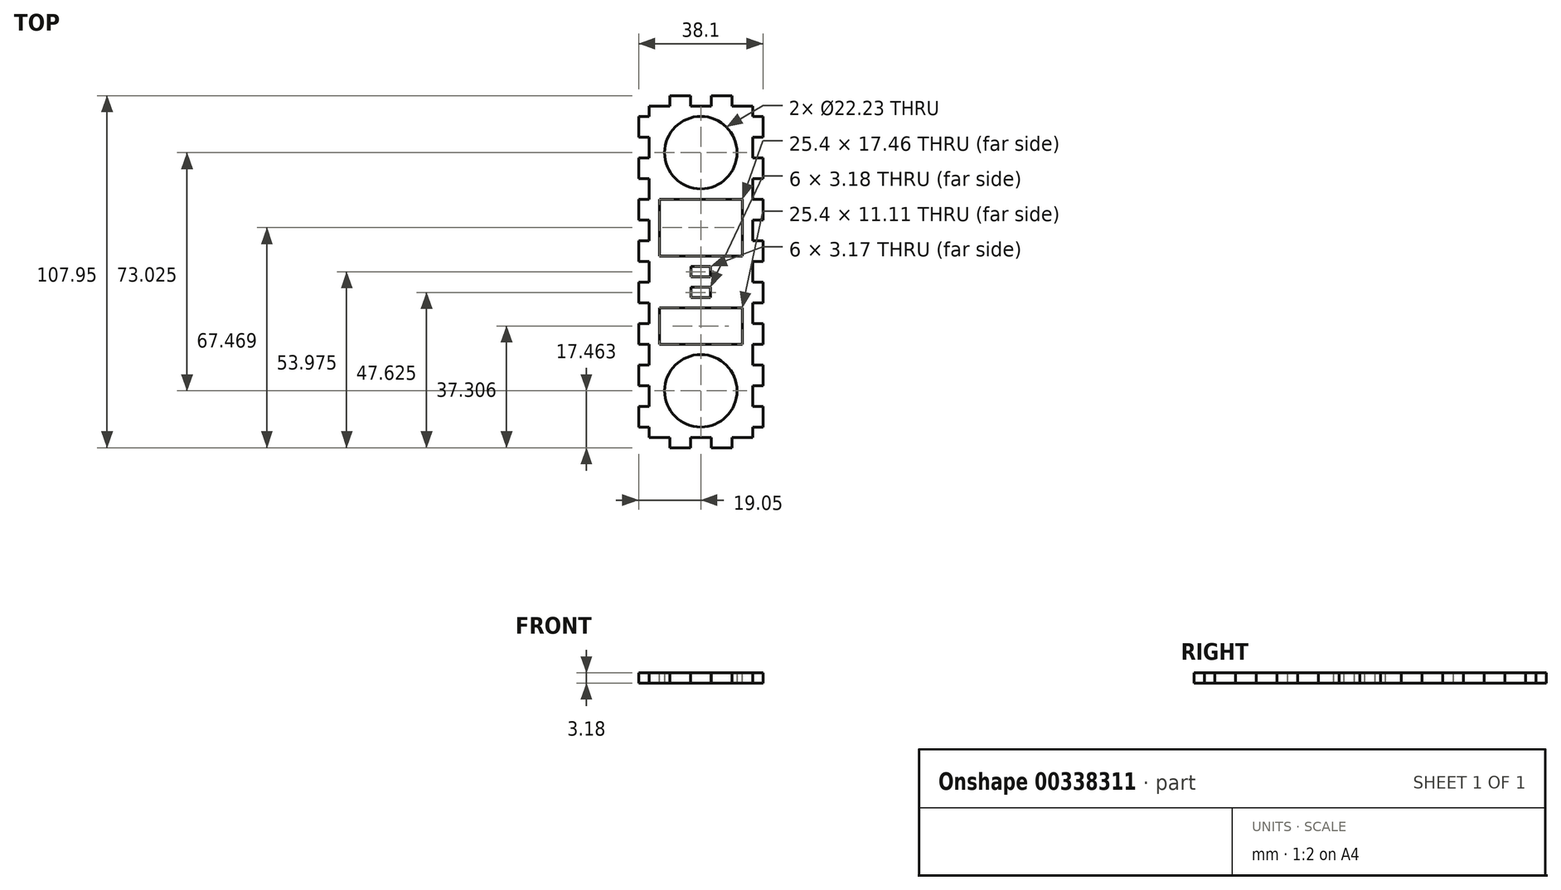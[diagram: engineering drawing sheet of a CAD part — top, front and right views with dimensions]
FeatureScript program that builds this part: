
annotation { "Feature Type Name" : "Feature", "Feature Type Description" : "" }
export const myFeature = defineFeature(function(context is Context, id is Id, definition is map)
    precondition{}
    {
        {
            var Q0;
            Q0=qCreatedBy(makeId("Top.planeOp"),FACE);
            var sketch = newSketch(context, id + "F0", { "sketchPlane" : qUnion([Q0])});
            skLineSegment(sketch, "E0.bottom", {"start": v(0, 0) * mm, "end": v(38.1, 0) * mm});
            skLineSegment(sketch, "E0.top", {"start": v(0, -107.95) * mm, "end": v(38.1, -107.95) * mm});
            skLineSegment(sketch, "E0.left", {"start": v(0, 0) * mm, "end": v(0, -107.95) * mm});
            skLineSegment(sketch, "E0.right", {"start": v(38.1, 0) * mm, "end": v(38.1, -107.95) * mm});
            skLineSegment(sketch, "E1", {"start": v(19.05, 0) * mm, "end": v(19.05, -17.46) * mm, "construction": true});
            skCircle(sketch, "E2", {"center": v(19.05, -17.46) * mm, "radius": 11.11 * mm});
            skLineSegment(sketch, "E3", {"start": v(19.05, -17.46) * mm, "end": v(19.05, -90.49) * mm, "construction": true});
            skLineSegment(sketch, "E4", {"start": v(19.05, -90.49) * mm, "end": v(19.05, -107.95) * mm, "construction": true});
            skCircle(sketch, "E5", {"center": v(19.05, -90.49) * mm, "radius": 11.11 * mm});
            skSolve(sketch);
        }
        {
            var Q0;
            Q0=qSketchRegion(id+"F0",true);
            extrude(context, id + "F1", {"entities" : qUnion([Q0]), "depth" : 3.17 * mm});
        }
        {
            var Q0;
            Q0=makeQuery(id+"F1.opExtrude","CAP_FACE",FACE,{"disambiguationData":[OSD([sQuery(id+"F0.wireOp",EDGE,"E0.bottom"),sQuery(id+"F0.wireOp",EDGE,"E0.top"),sQuery(id+"F0.wireOp",EDGE,"E0.left"),sQuery(id+"F0.wireOp",EDGE,"E0.right"),sQuery(id+"F0.wireOp",EDGE,"E2"),sQuery(id+"F0.wireOp",EDGE,"E5")])],"isStart":false});
            var sketch = newSketch(context, id + "F2", { "sketchPlane" : qUnion([Q0])});
            skLineSegment(sketch, "E6.bottom", {"start": v(38.1, 0) * mm, "end": v(34.93, 0) * mm});
            skLineSegment(sketch, "E6.top", {"start": v(38.1, -6.35) * mm, "end": v(34.93, -6.35) * mm});
            skLineSegment(sketch, "E6.left", {"start": v(38.1, 0) * mm, "end": v(38.1, -6.35) * mm});
            skLineSegment(sketch, "E6.right", {"start": v(34.93, 0) * mm, "end": v(34.93, -6.35) * mm});
            skLineSegment(sketch, "E7.bottom", {"start": v(0, 0) * mm, "end": v(3.17, 0) * mm});
            skLineSegment(sketch, "E7.top", {"start": v(0, -6.35) * mm, "end": v(3.17, -6.35) * mm});
            skLineSegment(sketch, "E7.left", {"start": v(0, 0) * mm, "end": v(0, -6.35) * mm});
            skLineSegment(sketch, "E7.right", {"start": v(3.17, 0) * mm, "end": v(3.17, -6.35) * mm});
            skLineSegment(sketch, "E8", {"start": v(3.17, -6.35) * mm, "end": v(3.17, -12.7) * mm, "construction": true});
            skLineSegment(sketch, "E9.bottom", {"start": v(3.17, -12.7) * mm, "end": v(0, -12.7) * mm});
            skLineSegment(sketch, "E9.top", {"start": v(3.17, -19.05) * mm, "end": v(0, -19.05) * mm});
            skLineSegment(sketch, "E9.left", {"start": v(3.17, -12.7) * mm, "end": v(3.17, -19.05) * mm});
            skLineSegment(sketch, "E9.right", {"start": v(0, -12.7) * mm, "end": v(0, -19.05) * mm});
            skLineSegment(sketch, "E10", {"start": v(34.93, -6.35) * mm, "end": v(34.93, -12.7) * mm, "construction": true});
            skLineSegment(sketch, "E11.bottom", {"start": v(34.93, -12.7) * mm, "end": v(38.1, -12.7) * mm});
            skLineSegment(sketch, "E11.top", {"start": v(34.93, -19.05) * mm, "end": v(38.1, -19.05) * mm});
            skLineSegment(sketch, "E11.left", {"start": v(34.93, -12.7) * mm, "end": v(34.93, -19.05) * mm});
            skLineSegment(sketch, "E11.right", {"start": v(38.1, -12.7) * mm, "end": v(38.1, -19.05) * mm});
            skLineSegment(sketch, "E12.0.1.0", {"start": v(34.93, -25.4) * mm, "end": v(38.1, -25.4) * mm});
            skLineSegment(sketch, "E12.0.1.1", {"start": v(34.93, -31.75) * mm, "end": v(38.1, -31.75) * mm});
            skLineSegment(sketch, "E12.0.1.2", {"start": v(34.93, -19.05) * mm, "end": v(34.93, -25.4) * mm, "construction": true});
            skLineSegment(sketch, "E12.0.1.3", {"start": v(38.1, -25.4) * mm, "end": v(38.1, -31.75) * mm});
            skLineSegment(sketch, "E12.0.1.4", {"start": v(34.93, -25.4) * mm, "end": v(34.93, -31.75) * mm});
            skLineSegment(sketch, "E12.0.2.0", {"start": v(34.93, -38.1) * mm, "end": v(38.1, -38.1) * mm});
            skLineSegment(sketch, "E12.0.2.1", {"start": v(34.93, -44.45) * mm, "end": v(38.1, -44.45) * mm});
            skLineSegment(sketch, "E12.0.2.2", {"start": v(34.93, -31.75) * mm, "end": v(34.93, -38.1) * mm, "construction": true});
            skLineSegment(sketch, "E12.0.2.3", {"start": v(38.1, -38.1) * mm, "end": v(38.1, -44.45) * mm});
            skLineSegment(sketch, "E12.0.2.4", {"start": v(34.93, -38.1) * mm, "end": v(34.93, -44.45) * mm});
            skLineSegment(sketch, "E12.0.3.0", {"start": v(34.93, -50.8) * mm, "end": v(38.1, -50.8) * mm});
            skLineSegment(sketch, "E12.0.3.1", {"start": v(34.93, -57.15) * mm, "end": v(38.1, -57.15) * mm});
            skLineSegment(sketch, "E12.0.3.2", {"start": v(34.93, -44.45) * mm, "end": v(34.93, -50.8) * mm, "construction": true});
            skLineSegment(sketch, "E12.0.3.3", {"start": v(38.1, -50.8) * mm, "end": v(38.1, -57.15) * mm});
            skLineSegment(sketch, "E12.0.3.4", {"start": v(34.93, -50.8) * mm, "end": v(34.93, -57.15) * mm});
            skLineSegment(sketch, "E12.0.4.0", {"start": v(34.93, -63.5) * mm, "end": v(38.1, -63.5) * mm});
            skLineSegment(sketch, "E12.0.4.1", {"start": v(34.93, -69.85) * mm, "end": v(38.1, -69.85) * mm});
            skLineSegment(sketch, "E12.0.4.2", {"start": v(34.93, -57.15) * mm, "end": v(34.93, -63.5) * mm, "construction": true});
            skLineSegment(sketch, "E12.0.4.3", {"start": v(38.1, -63.5) * mm, "end": v(38.1, -69.85) * mm});
            skLineSegment(sketch, "E12.0.4.4", {"start": v(34.93, -63.5) * mm, "end": v(34.93, -69.85) * mm});
            skLineSegment(sketch, "E12.0.5.0", {"start": v(34.93, -76.2) * mm, "end": v(38.1, -76.2) * mm});
            skLineSegment(sketch, "E12.0.5.1", {"start": v(34.93, -82.55) * mm, "end": v(38.1, -82.55) * mm});
            skLineSegment(sketch, "E12.0.5.2", {"start": v(34.93, -69.85) * mm, "end": v(34.93, -76.2) * mm, "construction": true});
            skLineSegment(sketch, "E12.0.5.3", {"start": v(38.1, -76.2) * mm, "end": v(38.1, -82.55) * mm});
            skLineSegment(sketch, "E12.0.5.4", {"start": v(34.93, -76.2) * mm, "end": v(34.93, -82.55) * mm});
            skLineSegment(sketch, "E12.0.6.0", {"start": v(34.93, -88.9) * mm, "end": v(38.1, -88.9) * mm});
            skLineSegment(sketch, "E12.0.6.1", {"start": v(34.93, -95.25) * mm, "end": v(38.1, -95.25) * mm});
            skLineSegment(sketch, "E12.0.6.2", {"start": v(34.93, -82.55) * mm, "end": v(34.93, -88.9) * mm, "construction": true});
            skLineSegment(sketch, "E12.0.6.3", {"start": v(38.1, -88.9) * mm, "end": v(38.1, -95.25) * mm});
            skLineSegment(sketch, "E12.0.6.4", {"start": v(34.93, -88.9) * mm, "end": v(34.93, -95.25) * mm});
            skLineSegment(sketch, "E12.0.7.0", {"start": v(34.93, -101.6) * mm, "end": v(38.1, -101.6) * mm});
            skLineSegment(sketch, "E12.0.7.1", {"start": v(34.93, -107.95) * mm, "end": v(38.1, -107.95) * mm});
            skLineSegment(sketch, "E12.0.7.2", {"start": v(34.93, -95.25) * mm, "end": v(34.93, -101.6) * mm, "construction": true});
            skLineSegment(sketch, "E12.0.7.3", {"start": v(38.1, -101.6) * mm, "end": v(38.1, -107.95) * mm});
            skLineSegment(sketch, "E12.0.7.4", {"start": v(34.93, -101.6) * mm, "end": v(34.93, -107.95) * mm});
            skLineSegment(sketch, "E12.0.8.0", {"start": v(34.93, -114.3) * mm, "end": v(38.1, -114.3) * mm});
            skLineSegment(sketch, "E12.0.8.1", {"start": v(34.93, -120.65) * mm, "end": v(38.1, -120.65) * mm});
            skLineSegment(sketch, "E12.0.8.2", {"start": v(34.93, -107.95) * mm, "end": v(34.93, -114.3) * mm, "construction": true});
            skLineSegment(sketch, "E12.0.8.3", {"start": v(38.1, -114.3) * mm, "end": v(38.1, -120.65) * mm});
            skLineSegment(sketch, "E12.0.8.4", {"start": v(34.93, -114.3) * mm, "end": v(34.93, -120.65) * mm});
            skLineSegment(sketch, "E12.0.9.0", {"start": v(34.93, -127) * mm, "end": v(38.1, -127) * mm});
            skLineSegment(sketch, "E12.0.9.1", {"start": v(34.93, -133.35) * mm, "end": v(38.1, -133.35) * mm});
            skLineSegment(sketch, "E12.0.9.2", {"start": v(34.93, -120.65) * mm, "end": v(34.93, -127) * mm, "construction": true});
            skLineSegment(sketch, "E12.0.9.3", {"start": v(38.1, -127) * mm, "end": v(38.1, -133.35) * mm});
            skLineSegment(sketch, "E12.0.9.4", {"start": v(34.93, -127) * mm, "end": v(34.93, -133.35) * mm});
            skLineSegment(sketch, "E12.direction1", {"start": v(17.46, -19.05) * mm, "end": v(34.93, -19.05) * mm, "construction": true});
            skLineSegment(sketch, "E12.direction2", {"start": v(34.93, -19.05) * mm, "end": v(34.93, -31.75) * mm, "construction": true});
            skLineSegment(sketch, "E13.0.1.0", {"start": v(3.17, -19.05) * mm, "end": v(3.17, -25.4) * mm, "construction": true});
            skLineSegment(sketch, "E13.0.1.1", {"start": v(3.17, -25.4) * mm, "end": v(0, -25.4) * mm});
            skLineSegment(sketch, "E13.0.1.2", {"start": v(3.17, -31.75) * mm, "end": v(0, -31.75) * mm});
            skLineSegment(sketch, "E13.0.1.3", {"start": v(3.17, -25.4) * mm, "end": v(3.17, -31.75) * mm});
            skLineSegment(sketch, "E13.0.1.4", {"start": v(0, -25.4) * mm, "end": v(0, -31.75) * mm});
            skLineSegment(sketch, "E13.0.2.0", {"start": v(3.17, -31.75) * mm, "end": v(3.17, -38.1) * mm, "construction": true});
            skLineSegment(sketch, "E13.0.2.1", {"start": v(3.17, -38.1) * mm, "end": v(0, -38.1) * mm});
            skLineSegment(sketch, "E13.0.2.2", {"start": v(3.17, -44.45) * mm, "end": v(0, -44.45) * mm});
            skLineSegment(sketch, "E13.0.2.3", {"start": v(3.17, -38.1) * mm, "end": v(3.17, -44.45) * mm});
            skLineSegment(sketch, "E13.0.2.4", {"start": v(0, -38.1) * mm, "end": v(0, -44.45) * mm});
            skLineSegment(sketch, "E13.0.3.0", {"start": v(3.17, -44.45) * mm, "end": v(3.17, -50.8) * mm, "construction": true});
            skLineSegment(sketch, "E13.0.3.1", {"start": v(3.17, -50.8) * mm, "end": v(0, -50.8) * mm});
            skLineSegment(sketch, "E13.0.3.2", {"start": v(3.17, -57.15) * mm, "end": v(0, -57.15) * mm});
            skLineSegment(sketch, "E13.0.3.3", {"start": v(3.17, -50.8) * mm, "end": v(3.17, -57.15) * mm});
            skLineSegment(sketch, "E13.0.3.4", {"start": v(0, -50.8) * mm, "end": v(0, -57.15) * mm});
            skLineSegment(sketch, "E13.0.4.0", {"start": v(3.17, -57.15) * mm, "end": v(3.17, -63.5) * mm, "construction": true});
            skLineSegment(sketch, "E13.0.4.1", {"start": v(3.17, -63.5) * mm, "end": v(0, -63.5) * mm});
            skLineSegment(sketch, "E13.0.4.2", {"start": v(3.17, -69.85) * mm, "end": v(0, -69.85) * mm});
            skLineSegment(sketch, "E13.0.4.3", {"start": v(3.17, -63.5) * mm, "end": v(3.17, -69.85) * mm});
            skLineSegment(sketch, "E13.0.4.4", {"start": v(0, -63.5) * mm, "end": v(0, -69.85) * mm});
            skLineSegment(sketch, "E13.0.5.0", {"start": v(3.17, -69.85) * mm, "end": v(3.17, -76.2) * mm, "construction": true});
            skLineSegment(sketch, "E13.0.5.1", {"start": v(3.17, -76.2) * mm, "end": v(0, -76.2) * mm});
            skLineSegment(sketch, "E13.0.5.2", {"start": v(3.17, -82.55) * mm, "end": v(0, -82.55) * mm});
            skLineSegment(sketch, "E13.0.5.3", {"start": v(3.17, -76.2) * mm, "end": v(3.17, -82.55) * mm});
            skLineSegment(sketch, "E13.0.5.4", {"start": v(0, -76.2) * mm, "end": v(0, -82.55) * mm});
            skLineSegment(sketch, "E13.0.6.0", {"start": v(3.17, -82.55) * mm, "end": v(3.17, -88.9) * mm, "construction": true});
            skLineSegment(sketch, "E13.0.6.1", {"start": v(3.17, -88.9) * mm, "end": v(0, -88.9) * mm});
            skLineSegment(sketch, "E13.0.6.2", {"start": v(3.17, -95.25) * mm, "end": v(0, -95.25) * mm});
            skLineSegment(sketch, "E13.0.6.3", {"start": v(3.17, -88.9) * mm, "end": v(3.17, -95.25) * mm});
            skLineSegment(sketch, "E13.0.6.4", {"start": v(0, -88.9) * mm, "end": v(0, -95.25) * mm});
            skLineSegment(sketch, "E13.0.7.0", {"start": v(3.17, -95.25) * mm, "end": v(3.17, -101.6) * mm, "construction": true});
            skLineSegment(sketch, "E13.0.7.1", {"start": v(3.17, -101.6) * mm, "end": v(0, -101.6) * mm});
            skLineSegment(sketch, "E13.0.7.2", {"start": v(3.17, -107.95) * mm, "end": v(0, -107.95) * mm});
            skLineSegment(sketch, "E13.0.7.3", {"start": v(3.17, -101.6) * mm, "end": v(3.17, -107.95) * mm});
            skLineSegment(sketch, "E13.0.7.4", {"start": v(0, -101.6) * mm, "end": v(0, -107.95) * mm});
            skLineSegment(sketch, "E13.0.8.0", {"start": v(3.17, -107.95) * mm, "end": v(3.17, -114.3) * mm, "construction": true});
            skLineSegment(sketch, "E13.0.8.1", {"start": v(3.17, -114.3) * mm, "end": v(0, -114.3) * mm});
            skLineSegment(sketch, "E13.0.8.2", {"start": v(3.17, -120.65) * mm, "end": v(0, -120.65) * mm});
            skLineSegment(sketch, "E13.0.8.3", {"start": v(3.17, -114.3) * mm, "end": v(3.17, -120.65) * mm});
            skLineSegment(sketch, "E13.0.8.4", {"start": v(0, -114.3) * mm, "end": v(0, -120.65) * mm});
            skLineSegment(sketch, "E13.0.9.0", {"start": v(3.17, -120.65) * mm, "end": v(3.17, -127) * mm, "construction": true});
            skLineSegment(sketch, "E13.0.9.1", {"start": v(3.17, -127) * mm, "end": v(0, -127) * mm});
            skLineSegment(sketch, "E13.0.9.2", {"start": v(3.17, -133.35) * mm, "end": v(0, -133.35) * mm});
            skLineSegment(sketch, "E13.0.9.3", {"start": v(3.17, -127) * mm, "end": v(3.17, -133.35) * mm});
            skLineSegment(sketch, "E13.0.9.4", {"start": v(0, -127) * mm, "end": v(0, -133.35) * mm});
            skLineSegment(sketch, "E13.direction1", {"start": v(0, -19.05) * mm, "end": v(17.46, -19.05) * mm, "construction": true});
            skLineSegment(sketch, "E13.direction2", {"start": v(0, -19.05) * mm, "end": v(0, -31.75) * mm, "construction": true});
            skLineSegment(sketch, "E14", {"start": v(19.05, 0) * mm, "end": v(19.05, -17.46) * mm, "construction": true});
            skLineSegment(sketch, "E15", {"start": v(19.05, -17.46) * mm, "end": v(19.05, -31.75) * mm, "construction": true});
            skLineSegment(sketch, "E16.bottom", {"start": v(6.35, -31.75) * mm, "end": v(31.75, -31.75) * mm});
            skLineSegment(sketch, "E16.left", {"start": v(6.35, -31.75) * mm, "end": v(6.35, -49.21) * mm});
            skLineSegment(sketch, "E16.right", {"start": v(31.75, -31.75) * mm, "end": v(31.75, -49.21) * mm});
            skLineSegment(sketch, "E17", {"start": v(31.75, -40.48) * mm, "end": v(34.93, -40.48) * mm, "construction": true});
            skLineSegment(sketch, "E18", {"start": v(19.05, -76.2) * mm, "end": v(19.05, -90.49) * mm, "construction": true});
            skLineSegment(sketch, "E19", {"start": v(19.05, -90.49) * mm, "end": v(19.05, -107.95) * mm, "construction": true});
            skLineSegment(sketch, "E20", {"start": v(6.35, -49.21) * mm, "end": v(31.75, -49.21) * mm});
            skLineSegment(sketch, "E21.bottom", {"start": v(16.05, -52.39) * mm, "end": v(22.05, -52.39) * mm});
            skLineSegment(sketch, "E21.top", {"start": v(16.05, -55.56) * mm, "end": v(22.05, -55.56) * mm});
            skLineSegment(sketch, "E21.left", {"start": v(16.05, -52.39) * mm, "end": v(16.05, -55.56) * mm});
            skLineSegment(sketch, "E21.right", {"start": v(22.05, -52.39) * mm, "end": v(22.05, -55.56) * mm});
            skLineSegment(sketch, "E22", {"start": v(19.05, -52.39) * mm, "end": v(19.05, -49.21) * mm, "construction": true});
            skLineSegment(sketch, "E23", {"start": v(19.05, -55.56) * mm, "end": v(19.05, -58.74) * mm, "construction": true});
            skLineSegment(sketch, "E24.bottom", {"start": v(16.05, -58.74) * mm, "end": v(22.05, -58.74) * mm});
            skLineSegment(sketch, "E24.top", {"start": v(16.05, -61.91) * mm, "end": v(22.05, -61.91) * mm});
            skLineSegment(sketch, "E24.left", {"start": v(16.05, -58.74) * mm, "end": v(16.05, -61.91) * mm});
            skLineSegment(sketch, "E24.right", {"start": v(22.05, -58.74) * mm, "end": v(22.05, -61.91) * mm});
            skLineSegment(sketch, "E25", {"start": v(22.05, -53.97) * mm, "end": v(92.08, -53.97) * mm});
            skLineSegment(sketch, "E26", {"start": v(19.05, -61.91) * mm, "end": v(19.05, -65.09) * mm, "construction": true});
            skLineSegment(sketch, "E27", {"start": v(19.05, -17.46) * mm, "end": v(92.08, -17.46) * mm, "construction": true});
            skLineSegment(sketch, "E28", {"start": v(92.08, -17.46) * mm, "end": v(92.08, -90.49) * mm, "construction": true});
            skLineSegment(sketch, "E29", {"start": v(92.08, -90.49) * mm, "end": v(19.05, -90.49) * mm, "construction": true});
            skLineSegment(sketch, "E30.bottom", {"start": v(6.35, -65.09) * mm, "end": v(31.75, -65.09) * mm});
            skLineSegment(sketch, "E30.top", {"start": v(6.35, -76.2) * mm, "end": v(31.75, -76.2) * mm});
            skLineSegment(sketch, "E30.left", {"start": v(6.35, -65.09) * mm, "end": v(6.35, -76.2) * mm});
            skLineSegment(sketch, "E30.right", {"start": v(31.75, -65.09) * mm, "end": v(31.75, -76.2) * mm});
            skSolve(sketch);
        }
        {
            var Q0;
            Q0=qSketchRegion(id+"F2",true);
            var Q1;
            Q1=makeQuery(id+"F1.opExtrude","CAP_FACE",FACE,{"disambiguationData":[OSD([sQuery(id+"F0.wireOp",EDGE,"E0.bottom"),sQuery(id+"F0.wireOp",EDGE,"E0.top"),sQuery(id+"F0.wireOp",EDGE,"E0.left"),sQuery(id+"F0.wireOp",EDGE,"E0.right"),sQuery(id+"F0.wireOp",EDGE,"E2"),sQuery(id+"F0.wireOp",EDGE,"E5")])],"isStart":true});
            extrude(context, id + "F3", {"entities" : qUnion([Q0]), "operationType" : NewBodyOperationType.REMOVE, "endBound" : BoundingType.UP_TO_SURFACE, "oppositeDirection" : true, "endBoundEntityFace" : qUnion([Q1]), "depth" : 25.4 * mm});
        }
        {
            var Q0;
            Q0=makeQuery(id+"F1.opExtrude","CAP_FACE",FACE,{"disambiguationData":[OSD([sQuery(id+"F0.wireOp",EDGE,"E0.bottom"),sQuery(id+"F0.wireOp",EDGE,"E0.top"),sQuery(id+"F0.wireOp",EDGE,"E0.left"),sQuery(id+"F0.wireOp",EDGE,"E0.right"),sQuery(id+"F0.wireOp",EDGE,"E2"),sQuery(id+"F0.wireOp",EDGE,"E5")])],"isStart":false});
            var sketch = newSketch(context, id + "F4", { "sketchPlane" : qUnion([Q0])});
            skLineSegment(sketch, "E31.bottom", {"start": v(15.88, 0) * mm, "end": v(22.23, 0) * mm});
            skLineSegment(sketch, "E31.top", {"start": v(15.88, -3.18) * mm, "end": v(22.23, -3.18) * mm});
            skLineSegment(sketch, "E31.left", {"start": v(15.88, 0) * mm, "end": v(15.88, -3.18) * mm});
            skLineSegment(sketch, "E31.right", {"start": v(22.23, 0) * mm, "end": v(22.23, -3.18) * mm});
            skLineSegment(sketch, "E32.bottom", {"start": v(28.58, 0) * mm, "end": v(34.93, 0) * mm});
            skLineSegment(sketch, "E32.top", {"start": v(28.58, -3.18) * mm, "end": v(34.93, -3.18) * mm});
            skLineSegment(sketch, "E32.left", {"start": v(28.58, 0) * mm, "end": v(28.58, -3.18) * mm});
            skLineSegment(sketch, "E32.right", {"start": v(34.93, 0) * mm, "end": v(34.93, -3.18) * mm});
            skLineSegment(sketch, "E33", {"start": v(15.88, -3.18) * mm, "end": v(9.53, -3.18) * mm, "construction": true});
            skLineSegment(sketch, "E34", {"start": v(28.58, -3.18) * mm, "end": v(22.23, -3.18) * mm, "construction": true});
            skLineSegment(sketch, "E35.bottom", {"start": v(9.53, -3.18) * mm, "end": v(3.17, -3.18) * mm});
            skLineSegment(sketch, "E35.top", {"start": v(9.53, 0) * mm, "end": v(3.17, 0) * mm});
            skLineSegment(sketch, "E35.left", {"start": v(9.53, -3.18) * mm, "end": v(9.53, 0) * mm});
            skLineSegment(sketch, "E35.right", {"start": v(3.17, -3.18) * mm, "end": v(3.17, 0) * mm});
            skLineSegment(sketch, "E36.bottom", {"start": v(34.93, -107.95) * mm, "end": v(28.58, -107.95) * mm});
            skLineSegment(sketch, "E36.top", {"start": v(34.93, -104.78) * mm, "end": v(28.58, -104.78) * mm});
            skLineSegment(sketch, "E36.left", {"start": v(34.93, -107.95) * mm, "end": v(34.93, -104.78) * mm});
            skLineSegment(sketch, "E36.right", {"start": v(28.58, -107.95) * mm, "end": v(28.58, -104.78) * mm});
            skLineSegment(sketch, "E37.bottom", {"start": v(3.18, -107.95) * mm, "end": v(9.53, -107.95) * mm});
            skLineSegment(sketch, "E37.top", {"start": v(3.18, -104.78) * mm, "end": v(9.53, -104.78) * mm});
            skLineSegment(sketch, "E37.left", {"start": v(3.18, -107.95) * mm, "end": v(3.18, -104.78) * mm});
            skLineSegment(sketch, "E37.right", {"start": v(9.53, -107.95) * mm, "end": v(9.53, -104.78) * mm});
            skLineSegment(sketch, "E38.bottom", {"start": v(15.88, -107.95) * mm, "end": v(22.23, -107.95) * mm});
            skLineSegment(sketch, "E38.top", {"start": v(15.88, -104.78) * mm, "end": v(22.23, -104.78) * mm});
            skLineSegment(sketch, "E38.left", {"start": v(15.88, -107.95) * mm, "end": v(15.88, -104.78) * mm});
            skLineSegment(sketch, "E38.right", {"start": v(22.23, -107.95) * mm, "end": v(22.23, -104.78) * mm});
            skLineSegment(sketch, "E39", {"start": v(9.53, -104.78) * mm, "end": v(15.88, -104.78) * mm, "construction": true});
            skLineSegment(sketch, "E40", {"start": v(22.23, -104.78) * mm, "end": v(28.58, -104.78) * mm, "construction": true});
            skSolve(sketch);
        }
        {
            var Q0;
            Q0=qSketchRegion(id+"F4",true);
            var Q1;
            Q1=makeQuery(id+"F1.opExtrude","CAP_FACE",FACE,{"disambiguationData":[OSD([sQuery(id+"F0.wireOp",EDGE,"E0.bottom"),sQuery(id+"F0.wireOp",EDGE,"E0.top"),sQuery(id+"F0.wireOp",EDGE,"E0.left"),sQuery(id+"F0.wireOp",EDGE,"E0.right"),sQuery(id+"F0.wireOp",EDGE,"E2"),sQuery(id+"F0.wireOp",EDGE,"E5")])],"isStart":true});
            extrude(context, id + "F5", {"entities" : qUnion([Q0]), "operationType" : NewBodyOperationType.REMOVE, "endBound" : BoundingType.UP_TO_SURFACE, "oppositeDirection" : true, "endBoundEntityFace" : qUnion([Q1]), "depth" : 25.4 * mm});
        }
    });
